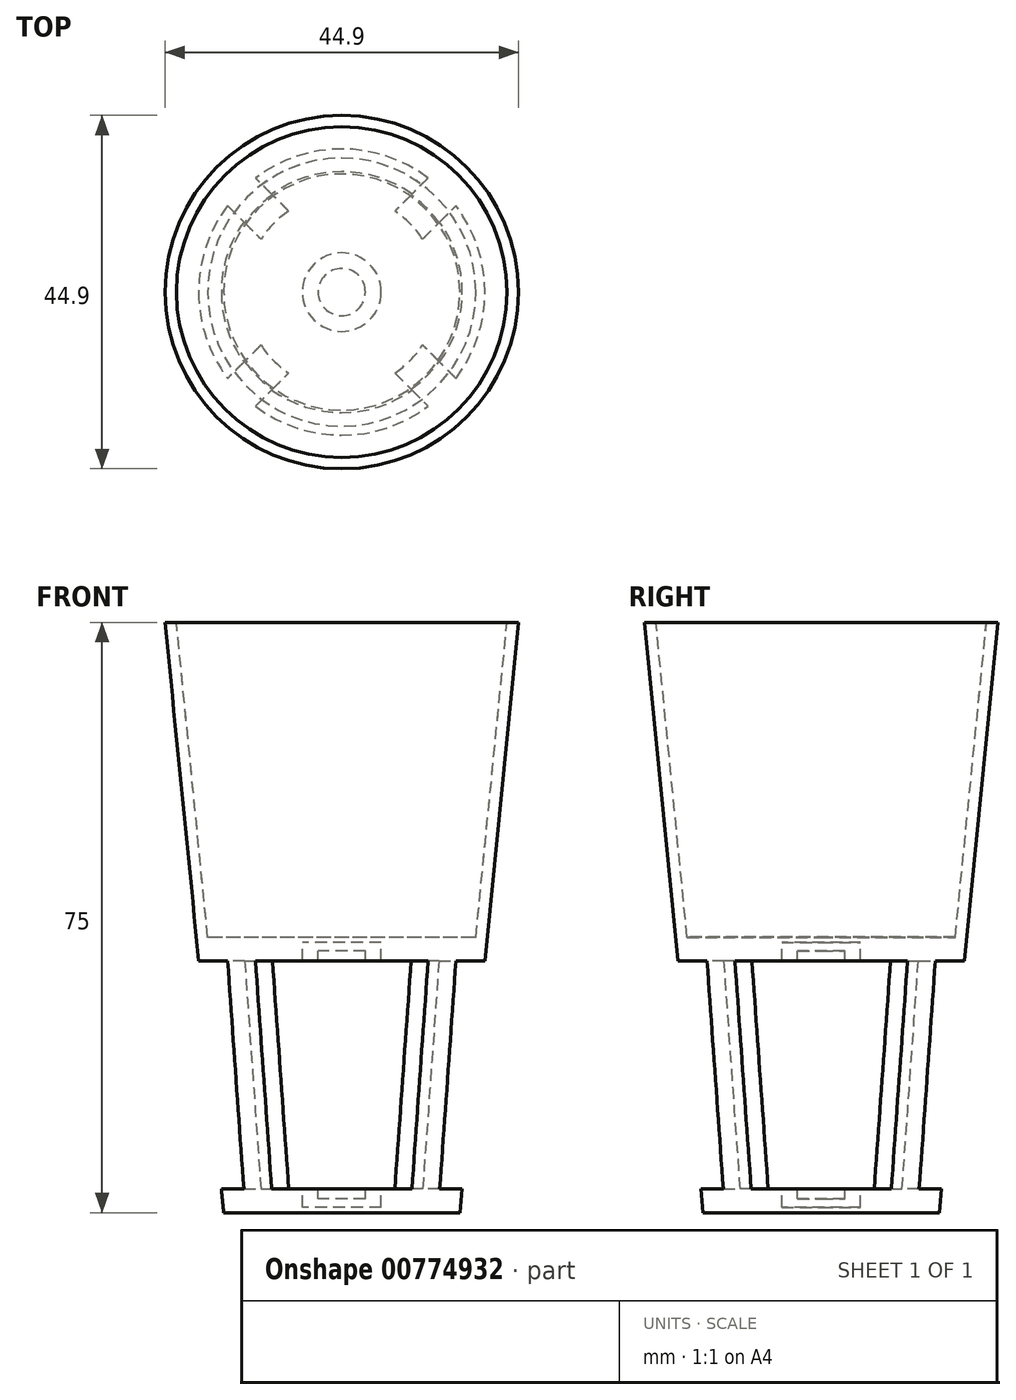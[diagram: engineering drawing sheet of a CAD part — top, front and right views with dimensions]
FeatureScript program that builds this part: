
annotation { "Feature Type Name" : "Feature", "Feature Type Description" : "" }
export const myFeature = defineFeature(function(context is Context, id is Id, definition is map)
    precondition{}
    {
        {
            var Q0;
            Q0=qCreatedBy(makeId("Front.planeOp"),FACE);
            var sketch = newSketch(context, id + "F0", { "sketchPlane" : qUnion([Q0])});
            skLineSegment(sketch, "E0", {"start": v(0, 0) * mm, "end": v(15, 0) * mm});
            skLineSegment(sketch, "E1", {"start": v(15, 0) * mm, "end": v(22.45, 75) * mm});
            skLineSegment(sketch, "E2", {"start": v(22.45, 75) * mm, "end": v(21, 75) * mm});
            skLineSegment(sketch, "E3", {"start": v(21, 75) * mm, "end": v(17.03, 35) * mm});
            skLineSegment(sketch, "E4", {"start": v(17.03, 35) * mm, "end": v(0, 35) * mm});
            skLineSegment(sketch, "E5", {"start": v(12.28, 3) * mm, "end": v(15.16, 32) * mm});
            skLineSegment(sketch, "E6", {"start": v(15.16, 32) * mm, "end": v(0, 32) * mm});
            skLineSegment(sketch, "E7", {"start": v(12.28, 3) * mm, "end": v(0, 3) * mm});
            skLineSegment(sketch, "E8.trimOffspring", {"start": v(0, 3) * mm, "end": v(0, 0) * mm});
            skLineSegment(sketch, "E9", {"start": v(0, 32) * mm, "end": v(0, 35) * mm});
            skSolve(sketch);
        }
        {
            var Q0;
            Q0=qSketchRegion(id+"F0",true);
            var Q1;
            Q1=sQuery(id+"F0.wireOp",EDGE,"E9");
            revolve(context, id + "F1", {"surfaceOperationType" : NewSurfaceOperationType.NEW, "entities" : qUnion([Q0]), "axis" : qUnion([Q1]), "revolveType" : RevolveType.FULL});
        }
        {
            var Q0;
            Q0=makeQuery(id+"F1.opRevolve","SWEPT_FACE",FACE,{"disambiguationData":[OSD([sQuery(id+"F0.wireOp",EDGE,"E7")])]});
            var sketch = newSketch(context, id + "F2", { "sketchPlane" : qUnion([Q0])});
            skArc(sketch, "E10", {"start": v(15.68, 19.22) * mm, "mid": v(0, 24.8) * mm, "end": v(-15.68, 19.22) * mm});
            skLineSegment(sketch, "E11", {"start": v(0, 0) * mm, "end": v(0, 28.4) * mm, "construction": true});
            skLineSegment(sketch, "E12", {"start": v(0, 0) * mm, "end": v(28.58, 0) * mm, "construction": true});
            skLineSegment(sketch, "E13", {"start": v(0, 0) * mm, "end": v(20.34, 20.34) * mm, "construction": true});
            skLineSegment(sketch, "E14", {"start": v(15.8, 12.26) * mm, "end": v(19.22, 15.68) * mm});
            skLineSegment(sketch, "E15.MirrorCS", {"start": v(12.26, 15.8) * mm, "end": v(15.68, 19.22) * mm});
            skLineSegment(sketch, "E16.MirrorCS", {"start": v(-15.8, 12.26) * mm, "end": v(-19.22, 15.68) * mm});
            skLineSegment(sketch, "E17.MirrorCS", {"start": v(-12.26, 15.8) * mm, "end": v(-15.68, 19.22) * mm});
            skLineSegment(sketch, "E18.MirrorCS", {"start": v(12.26, -15.8) * mm, "end": v(15.68, -19.22) * mm});
            skLineSegment(sketch, "E19.MirrorCS", {"start": v(-12.26, -15.8) * mm, "end": v(-15.68, -19.22) * mm});
            skLineSegment(sketch, "E20.MirrorCS", {"start": v(15.8, -12.26) * mm, "end": v(19.22, -15.68) * mm});
            skLineSegment(sketch, "E21.MirrorCS", {"start": v(-15.8, -12.26) * mm, "end": v(-19.22, -15.68) * mm});
            skPoint(sketch, "E22.end.orphan", {"position": v(19.93, 19.93) * mm});
            skPoint(sketch, "E22.start.orphan", {"position": v(21.7, 18.16) * mm});
            skPoint(sketch, "E23.MirrorCS.start.orphan", {"position": v(18.16, 21.7) * mm});
            skPoint(sketch, "E24.orphan", {"position": v(-18.16, 21.7) * mm});
            skPoint(sketch, "E25.MirrorCS.end.orphan", {"position": v(-19.93, 19.93) * mm});
            skPoint(sketch, "E26.MirrorCS.start.orphan", {"position": v(-21.7, 18.16) * mm});
            skArc(sketch, "E27.trimOffspring", {"start": v(-19.22, 15.68) * mm, "mid": v(-24.8, 0) * mm, "end": v(-19.22, -15.68) * mm});
            skPoint(sketch, "E28.orphan", {"position": v(-18.16, -21.7) * mm});
            skPoint(sketch, "E29.MirrorCS.end.orphan", {"position": v(-19.93, -19.93) * mm});
            skPoint(sketch, "E30.MirrorCS.start.orphan", {"position": v(-21.7, -18.16) * mm});
            skArc(sketch, "E31.trimOffspring", {"start": v(-15.68, -19.22) * mm, "mid": v(0, -24.8) * mm, "end": v(15.68, -19.22) * mm});
            skPoint(sketch, "E32.MirrorCS.end.orphan", {"position": v(19.93, -19.93) * mm});
            skPoint(sketch, "E32.MirrorCS.start.orphan", {"position": v(21.7, -18.16) * mm});
            skPoint(sketch, "E33.MirrorCS.start.orphan", {"position": v(18.16, -21.7) * mm});
            skArc(sketch, "E34.trimOffspring", {"start": v(19.22, -15.68) * mm, "mid": v(24.8, 0) * mm, "end": v(19.22, 15.68) * mm});
            skArc(sketch, "E35", {"start": v(-8.61, 5.08) * mm, "mid": v(-10, 0) * mm, "end": v(-8.61, -5.08) * mm});
            skLineSegment(sketch, "E36", {"start": v(-12.26, -15.8) * mm, "end": v(-5.08, -8.61) * mm});
            skLineSegment(sketch, "E37", {"start": v(-15.8, -12.26) * mm, "end": v(-8.61, -5.08) * mm});
            skLineSegment(sketch, "E38", {"start": v(12.26, -15.8) * mm, "end": v(5.08, -8.61) * mm});
            skLineSegment(sketch, "E39", {"start": v(15.8, -12.26) * mm, "end": v(8.61, -5.08) * mm});
            skLineSegment(sketch, "E40", {"start": v(15.8, 12.26) * mm, "end": v(8.61, 5.08) * mm});
            skLineSegment(sketch, "E41", {"start": v(12.26, 15.8) * mm, "end": v(5.08, 8.61) * mm});
            skLineSegment(sketch, "E42", {"start": v(-12.26, 15.8) * mm, "end": v(-5.08, 8.61) * mm});
            skLineSegment(sketch, "E43", {"start": v(-15.8, 12.26) * mm, "end": v(-8.61, 5.08) * mm});
            skArc(sketch, "E44.trimOffspring", {"start": v(5.08, 8.61) * mm, "mid": v(0, 10) * mm, "end": v(-5.08, 8.61) * mm});
            skArc(sketch, "E45.trimOffspring", {"start": v(8.61, -5.08) * mm, "mid": v(10, 0) * mm, "end": v(8.61, 5.08) * mm});
            skArc(sketch, "E46.trimOffspring", {"start": v(-5.08, -8.61) * mm, "mid": v(0, -10) * mm, "end": v(5.08, -8.61) * mm});
            skSolve(sketch);
        }
        {
            var Q0;
            Q0=qSketchRegion(id+"F2",true);
            extrude(context, id + "F3", {"entities" : qUnion([Q0]), "operationType" : NewBodyOperationType.REMOVE, "depth" : 29 * mm, "offsetDistance" : 25 * mm});
        }
        {
            var Q0;
            Q0=makeQuery(id+"F3.boolean.opBoolean","MERGE",FACE,{"derivedFrom":[makeQuery(id+"F1.opRevolve","SWEPT_FACE",FACE,{"disambiguationData":[OSD([sQuery(id+"F0.wireOp",EDGE,"E7")])]}),makeQuery(id+"F3.opExtrude","CAP_FACE",FACE,{"disambiguationData":[OSD([sQuery(id+"F2.wireOp",EDGE,"E10"),sQuery(id+"F2.wireOp",EDGE,"E15.MirrorCS"),sQuery(id+"F2.wireOp",EDGE,"E17.MirrorCS"),sQuery(id+"F2.wireOp",EDGE,"E41"),sQuery(id+"F2.wireOp",EDGE,"E42"),sQuery(id+"F2.wireOp",EDGE,"E44.trimOffspring")])],"isStart":true}),makeQuery(id+"F3.opExtrude","CAP_FACE",FACE,{"disambiguationData":[OSD([sQuery(id+"F2.wireOp",EDGE,"E14"),sQuery(id+"F2.wireOp",EDGE,"E20.MirrorCS"),sQuery(id+"F2.wireOp",EDGE,"E34.trimOffspring"),sQuery(id+"F2.wireOp",EDGE,"E39"),sQuery(id+"F2.wireOp",EDGE,"E40"),sQuery(id+"F2.wireOp",EDGE,"E45.trimOffspring")])],"isStart":true}),makeQuery(id+"F3.opExtrude","CAP_FACE",FACE,{"disambiguationData":[OSD([sQuery(id+"F2.wireOp",EDGE,"E16.MirrorCS"),sQuery(id+"F2.wireOp",EDGE,"E21.MirrorCS"),sQuery(id+"F2.wireOp",EDGE,"E27.trimOffspring"),sQuery(id+"F2.wireOp",EDGE,"E35"),sQuery(id+"F2.wireOp",EDGE,"E37"),sQuery(id+"F2.wireOp",EDGE,"E43")])],"isStart":true}),makeQuery(id+"F3.opExtrude","CAP_FACE",FACE,{"disambiguationData":[OSD([sQuery(id+"F2.wireOp",EDGE,"E18.MirrorCS"),sQuery(id+"F2.wireOp",EDGE,"E19.MirrorCS"),sQuery(id+"F2.wireOp",EDGE,"E31.trimOffspring"),sQuery(id+"F2.wireOp",EDGE,"E36"),sQuery(id+"F2.wireOp",EDGE,"E38"),sQuery(id+"F2.wireOp",EDGE,"E46.trimOffspring")])],"isStart":true})]});
            var sketch = newSketch(context, id + "F4", { "sketchPlane" : qUnion([Q0])});
            skCircle(sketch, "E47", {"center": v(0, 0) * mm, "radius": 3.5 * mm});
            skSolve(sketch);
        }
        {
            var Q0;
            Q0=qCreatedBy(makeId("Front.planeOp"),FACE);
            var sketch = newSketch(context, id + "F5", { "sketchPlane" : qUnion([Q0])});
            skLineSegment(sketch, "E48", {"start": v(0, 33.25) * mm, "end": v(3, 33.25) * mm});
            skLineSegment(sketch, "E49", {"start": v(3, 33.25) * mm, "end": v(3, 29.12) * mm});
            skLineSegment(sketch, "E50", {"start": v(3, 29.12) * mm, "end": v(3, 29.12) * mm});
            skArc(sketch, "E51", {"start": v(3, 5.88) * mm, "mid": v(12, 17.5) * mm, "end": v(3, 29.12) * mm});
            skLineSegment(sketch, "E52", {"start": v(3, 5.88) * mm, "end": v(3, 1.75) * mm});
            skLineSegment(sketch, "E53", {"start": v(3, 1.75) * mm, "end": v(0, 1.75) * mm});
            skLineSegment(sketch, "E54.MirrorCS", {"start": v(0, 33.25) * mm, "end": v(-3, 33.25) * mm});
            skLineSegment(sketch, "E55.MirrorCS", {"start": v(-3, 33.25) * mm, "end": v(-3, 29.12) * mm});
            skLineSegment(sketch, "E56.MirrorCS", {"start": v(-3, 1.75) * mm, "end": v(0, 1.75) * mm});
            skLineSegment(sketch, "E57.MirrorCS", {"start": v(-3, 5.88) * mm, "end": v(-3, 1.75) * mm});
            skArc(sketch, "E58.MirrorCS", {"start": v(-3, 5.88) * mm, "mid": v(-12, 17.5) * mm, "end": v(-3, 29.12) * mm});
            skSolve(sketch);
        }
        {
            var Q0;
            Q0=qSketchRegion(id+"F5",true);
            extrude(context, id + "F6", {"entities" : qUnion([Q0]), "endBound" : BoundingType.SYMMETRIC, "depth" : 4 * mm, "offsetDistance" : 25 * mm});
        }
        {
            var Q0;
            Q0=qCreatedBy(makeId("Front.planeOp"),FACE);
            var sketch = newSketch(context, id + "F7", { "sketchPlane" : qUnion([Q0])});
            skLineSegment(sketch, "E59.0", {"start": v(3, 33.25) * mm, "end": v(3, 29.12) * mm});
            skLineSegment(sketch, "E60.0", {"start": v(0, 33.25) * mm, "end": v(3, 33.25) * mm});
            skLineSegment(sketch, "E61", {"start": v(0, 33.25) * mm, "end": v(0, 34.3) * mm});
            skLineSegment(sketch, "E62", {"start": v(0, 34.3) * mm, "end": v(5, 34.3) * mm});
            skLineSegment(sketch, "E63", {"start": v(5, 34.3) * mm, "end": v(5, 29.12) * mm});
            skLineSegment(sketch, "E64", {"start": v(5, 29.12) * mm, "end": v(3, 29.12) * mm});
            skLineSegment(sketch, "E65", {"start": v(0, 17.5) * mm, "end": v(16.9, 17.5) * mm, "construction": true});
            skLineSegment(sketch, "E66.MirrorCS", {"start": v(5, 5.88) * mm, "end": v(3, 5.88) * mm});
            skLineSegment(sketch, "E67.MirrorCS", {"start": v(5, 0.7) * mm, "end": v(5, 5.88) * mm});
            skLineSegment(sketch, "E68.MirrorCS", {"start": v(0, 0.7) * mm, "end": v(5, 0.7) * mm});
            skLineSegment(sketch, "E69.MirrorCS", {"start": v(3, 1.75) * mm, "end": v(3, 5.88) * mm});
            skLineSegment(sketch, "E70.MirrorCS", {"start": v(0, 1.75) * mm, "end": v(3, 1.75) * mm});
            skLineSegment(sketch, "E71.MirrorCS", {"start": v(0, 1.75) * mm, "end": v(0, 0.7) * mm});
            skSolve(sketch);
        }
        {
            var Q0;
            Q0=qSketchRegion(id+"F7",true);
            var Q1;
            Q1=sQuery(id+"F7.wireOp",EDGE,"E61");
            revolve(context, id + "F8", {"operationType" : NewBodyOperationType.REMOVE, "surfaceOperationType" : NewSurfaceOperationType.NEW, "entities" : qUnion([Q0]), "axis" : qUnion([Q1]), "revolveType" : RevolveType.FULL, "oppositeDirection" : true});
        }
        {
            var Q0;
            Q0=qCreatedBy(makeId("Front.planeOp"),FACE);
            var sketch = newSketch(context, id + "F9", { "sketchPlane" : qUnion([Q0])});
            skLineSegment(sketch, "E72", {"start": v(21, 74.98) * mm, "end": v(17.03, 34.98) * mm});
            skLineSegment(sketch, "E73", {"start": v(-17.03, 34.98) * mm, "end": v(-20.5, 69.95) * mm});
            skLineSegment(sketch, "E74", {"start": v(20.5, 69.95) * mm, "end": v(17.03, 34.98) * mm});
            skLineSegment(sketch, "E75", {"start": v(21, 74.98) * mm, "end": v(0, 74.98) * mm});
            skLineSegment(sketch, "E76", {"start": v(0, 74.98) * mm, "end": v(0, 34.98) * mm});
            skLineSegment(sketch, "E77", {"start": v(0, 34.98) * mm, "end": v(17.03, 34.98) * mm});
            skSolve(sketch);
        }
        {
            var Q0;
            {var subQ0=sQuery(id+"F9.wireOp",EDGE,"E75");Q0=makeQuery(id+"F9.imprint","IMPRINT",FACE,{"disambiguationData":[TD([[makeQuery(id+"F9.imprint","IMPRINT",EDGE,{"derivedFrom":subQ0}),1.0]])]});}
            var Q1;
            Q1=sQuery(id+"F9.wireOp",EDGE,"E76");
            revolve(context, id + "F10", {"surfaceOperationType" : NewSurfaceOperationType.NEW, "entities" : qUnion([Q0]), "axis" : qUnion([Q1]), "revolveType" : RevolveType.FULL});
        }
        {
            var Q0;
            Q0=makeQuery(id+"F6.opExtrude","SWEPT_BODY",BODY,{"disambiguationData":[OSD([sQuery(id+"F5.wireOp",EDGE,"E48"),sQuery(id+"F5.wireOp",EDGE,"E49"),sQuery(id+"F5.wireOp",EDGE,"E51"),sQuery(id+"F5.wireOp",EDGE,"E52"),sQuery(id+"F5.wireOp",EDGE,"E53"),sQuery(id+"F5.wireOp",EDGE,"E54.MirrorCS"),sQuery(id+"F5.wireOp",EDGE,"E55.MirrorCS"),sQuery(id+"F5.wireOp",EDGE,"E56.MirrorCS"),sQuery(id+"F5.wireOp",EDGE,"E57.MirrorCS"),sQuery(id+"F5.wireOp",EDGE,"E58.MirrorCS")])]});
            deleteBodies(context, id + "F11", {"entities" : qUnion([Q0])});
        }
    });
